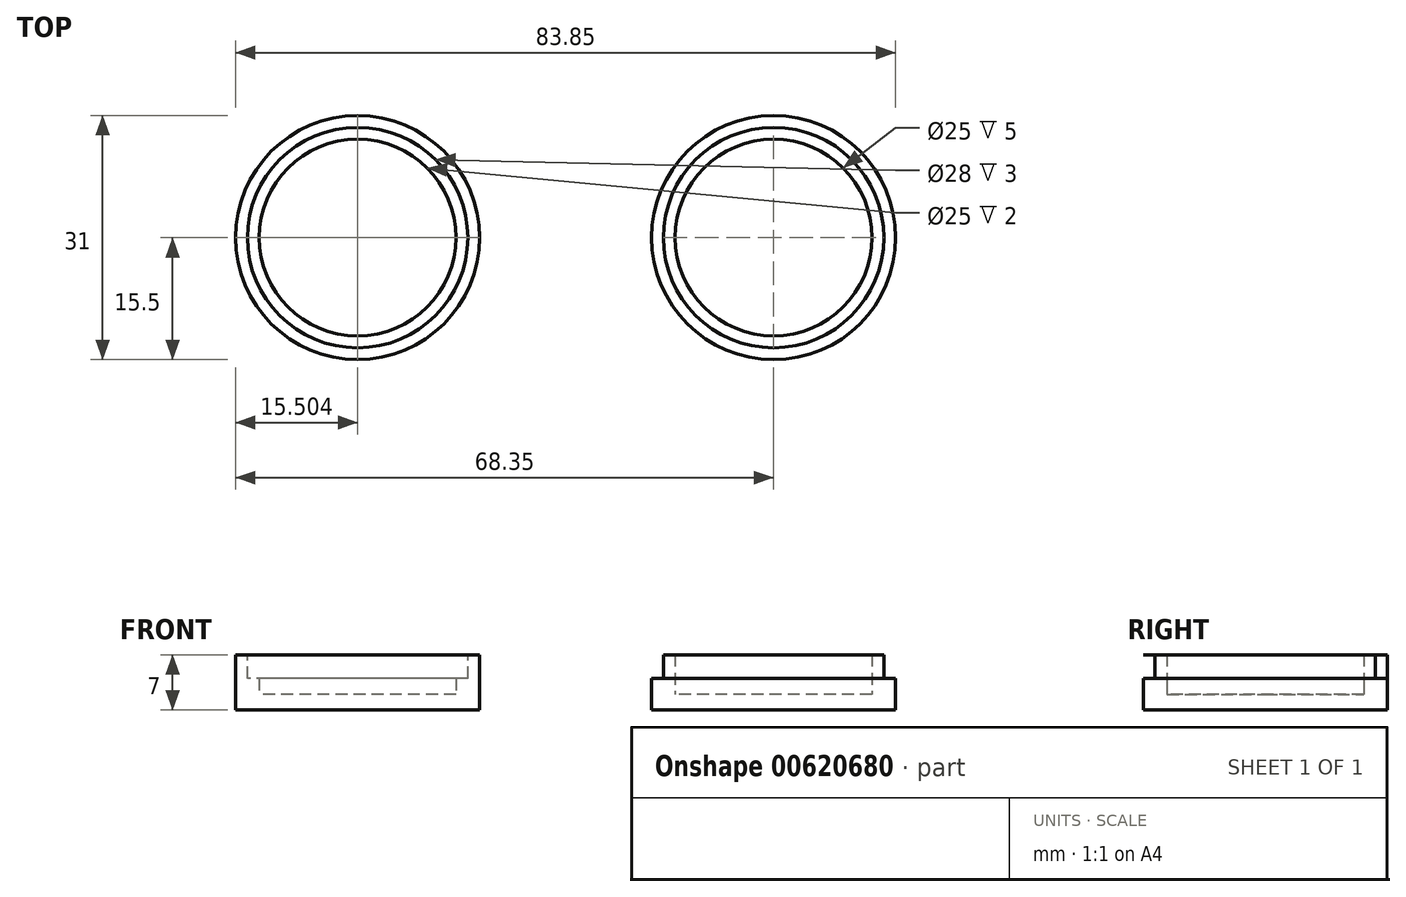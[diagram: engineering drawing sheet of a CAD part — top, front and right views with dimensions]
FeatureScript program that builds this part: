
annotation { "Feature Type Name" : "Feature", "Feature Type Description" : "" }
export const myFeature = defineFeature(function(context is Context, id is Id, definition is map)
    precondition{}
    {
        {
            var Q0;
            Q0=qCreatedBy(makeId("Top.planeOp"),FACE);
            var sketch = newSketch(context, id + "F0", { "sketchPlane" : qUnion([Q0])});
            skCircle(sketch, "E0", {"center": v(0, 0) * mm, "radius": 12.5 * mm});
            skCircle(sketch, "E1", {"center": v(-52.85, 0) * mm, "radius": 12.5 * mm});
            skCircle(sketch, "E2.0", {"center": v(-52.85, 0) * mm, "radius": 15.5 * mm});
            skCircle(sketch, "E3.0", {"center": v(0, 0) * mm, "radius": 15.5 * mm});
            skSolve(sketch);
        }
        {
            var Q0;
            Q0=makeQuery(id+"F0.imprint","IMPRINT",FACE,{"disambiguationData":[TD([[makeQuery(id+"F0.imprint","IMPRINT",EDGE,{"derivedFrom":sQuery(id+"F0.wireOp",EDGE,"E1")}),-1.0]])]});
            var Q1;
            Q1=makeQuery(id+"F0.imprint","IMPRINT",FACE,{"disambiguationData":[TD([[makeQuery(id+"F0.imprint","IMPRINT",EDGE,{"derivedFrom":sQuery(id+"F0.wireOp",EDGE,"E0")}),-1.0]])]});
            extrude(context, id + "F1", {"entities" : qUnion([Q0, Q1]), "depth" : 7 * mm, "offsetDistance" : 25 * mm});
        }
        {
            var Q0;
            Q0=qCreatedBy(makeId("Top.planeOp"),FACE);
            var sketch = newSketch(context, id + "F2", { "sketchPlane" : qUnion([Q0])});
            skCircle(sketch, "E4.0", {"center": v(-52.85, 0) * mm, "radius": 12.5 * mm});
            skCircle(sketch, "E4.1", {"center": v(0, 0) * mm, "radius": 12.5 * mm});
            skSolve(sketch);
        }
        {
            var Q0;
            Q0 = qSketchRegion(id + "F2", true);
            extrude(context, id + "F3", {"entities" : qUnion([Q0]), "operationType" : NewBodyOperationType.ADD, "depth" : 2 * mm, "offsetDistance" : 25 * mm});
        }
        {
            var Q0;
            Q0=makeQuery(id+"F1.opExtrude","CAP_FACE",FACE,{"disambiguationData":[OSD([sQuery(id+"F0.wireOp",EDGE,"E1"),sQuery(id+"F0.wireOp",EDGE,"E2.0")])],"isStart":false});
            var sketch = newSketch(context, id + "F4", { "sketchPlane" : qUnion([Q0])});
            skCircle(sketch, "E5.1.0", {"center": v(0, 0) * mm, "radius": 15.5 * mm});
            skCircle(sketch, "E6.0", {"center": v(-52.85, 0) * mm, "radius": 14 * mm});
            skCircle(sketch, "E7.0", {"center": v(0, 0) * mm, "radius": 14 * mm});
            skCircle(sketch, "E8.0", {"center": v(-52.85, 0) * mm, "radius": 12.5 * mm});
            skCircle(sketch, "E8.1", {"center": v(0, 0) * mm, "radius": 12.5 * mm});
            skCircle(sketch, "E9.0", {"center": v(-52.85, 0) * mm, "radius": 15.5 * mm});
            skSolve(sketch);
        }
        {
            var Q0;
            Q0=makeQuery(id+"F4.imprint","IMPRINT",FACE,{"disambiguationData":[TD([[makeQuery(id+"F4.imprint","IMPRINT",EDGE,{"derivedFrom":sQuery(id+"F4.wireOp",EDGE,"E6.0")}),1.0]])]});
            var Q1;
            Q1=makeQuery(id+"F4.imprint","IMPRINT",FACE,{"disambiguationData":[TD([[makeQuery(id+"F4.imprint","IMPRINT",EDGE,{"derivedFrom":sQuery(id+"F4.wireOp",EDGE,"E5.1.0")}),1.0]])]});
            extrude(context, id + "F5", {"entities" : qUnion([Q0, Q1]), "operationType" : NewBodyOperationType.REMOVE, "oppositeDirection" : true, "depth" : 3 * mm, "offsetDistance" : 25 * mm});
        }
        {
            var Q0;
            Q0=makeQuery(id+"F1.opExtrude","CAP_FACE",FACE,{"disambiguationData":[OSD([sQuery(id+"F0.wireOp",EDGE,"E0"),sQuery(id+"F0.wireOp",EDGE,"E3.0")])],"isStart":false});
            var sketch = newSketch(context, id + "F6", { "sketchPlane" : qUnion([Q0])});
            skCircle(sketch, "E10.0", {"center": v(0, 0) * mm, "radius": 14 * mm});
            skCircle(sketch, "E11.0", {"center": v(0, 0) * mm, "radius": 15.5 * mm});
            skSolve(sketch);
        }
        {
            var Q0;
            Q0=makeQuery(id+"F6.imprint","IMPRINT",FACE,{"disambiguationData":[TD([[makeQuery(id+"F6.imprint","IMPRINT",EDGE,{"derivedFrom":sQuery(id+"F6.wireOp",EDGE,"E10.0")}),-1.0]])]});
            extrude(context, id + "F7", {"entities" : qUnion([Q0]), "operationType" : NewBodyOperationType.REMOVE, "oppositeDirection" : true, "depth" : 3 * mm, "offsetDistance" : 25 * mm});
        }
    });
